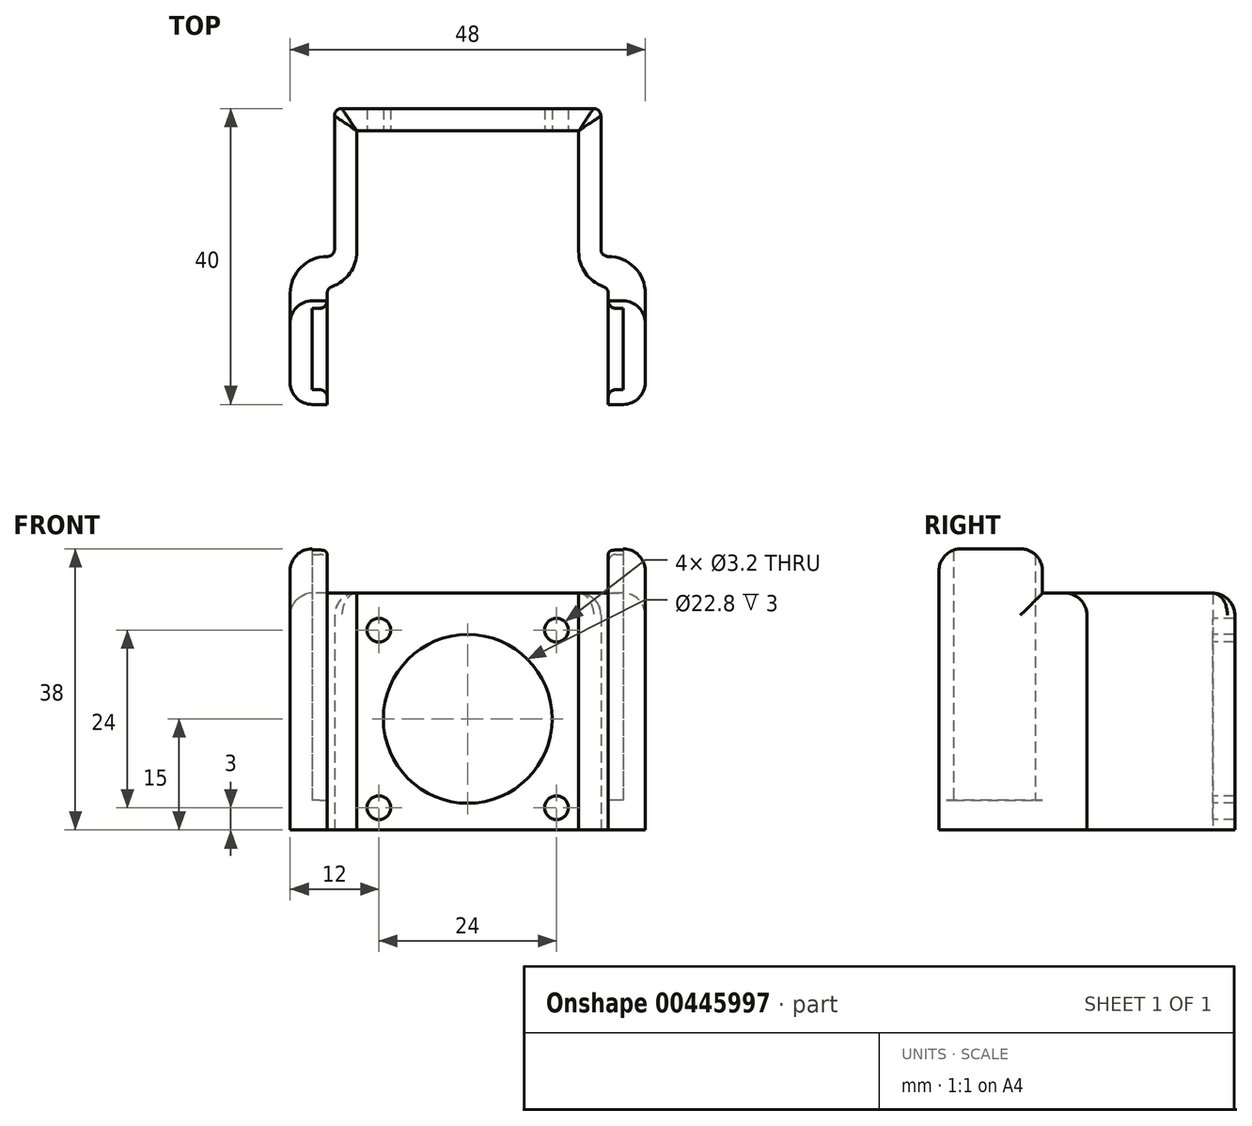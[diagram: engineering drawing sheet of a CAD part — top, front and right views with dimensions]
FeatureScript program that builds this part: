
annotation { "Feature Type Name" : "Feature", "Feature Type Description" : "" }
export const myFeature = defineFeature(function(context is Context, id is Id, definition is map)
    precondition{}
    {
        {
            var Q0;
            Q0=qCreatedBy(makeId("Top.planeOp"),FACE);
            var sketch = newSketch(context, id + "F0", { "sketchPlane" : qUnion([Q0])});
            skLineSegment(sketch, "E0", {"start": v(-29.4, 0) * mm, "end": v(-18, 0) * mm, "construction": true});
            skLineSegment(sketch, "E1.0", {"start": v(-29.4, -20) * mm, "end": v(-19, -20) * mm, "construction": true});
            skLineSegment(sketch, "E2.0", {"start": v(-18, 20) * mm, "end": v(0, 20) * mm, "construction": true});
            skLineSegment(sketch, "E3", {"start": v(0, 32.75) * mm, "end": v(0, -30.7) * mm, "construction": true});
            skLineSegment(sketch, "E4.0", {"start": v(-18, 32.75) * mm, "end": v(-18, 0) * mm, "construction": true});
            skLineSegment(sketch, "E5.trimOffspring", {"start": v(-24, 0) * mm, "end": v(-24, -30.7) * mm, "construction": true});
            skLineSegment(sketch, "E6.0", {"start": v(-15, 17) * mm, "end": v(0, 17) * mm});
            skLineSegment(sketch, "E7.0", {"start": v(-15, 32.75) * mm, "end": v(-15, 20) * mm});
            skLineSegment(sketch, "E8.trimOffspring", {"start": v(-15, 17) * mm, "end": v(-15, 0) * mm});
            skLineSegment(sketch, "E9.0", {"start": v(-29.4, -4) * mm, "end": v(-24, -4) * mm, "construction": true});
            skLineSegment(sketch, "E10", {"start": v(-15, 0) * mm, "end": v(-15, -8.6) * mm, "construction": true});
            skLineSegment(sketch, "E11.0", {"start": v(-21, -4) * mm, "end": v(-21, -30.7) * mm, "construction": true});
            skLineSegment(sketch, "E12.trimOffspring", {"start": v(-21, -4) * mm, "end": v(-15, -4) * mm, "construction": true});
            skLineSegment(sketch, "E13.trimOffspring", {"start": v(-15, 0) * mm, "end": v(35.32, 0) * mm, "construction": true});
            skLineSegment(sketch, "E14.0", {"start": v(-19, -5) * mm, "end": v(-19, -30.7) * mm, "construction": true});
            skLineSegment(sketch, "E15", {"start": v(-24, -20) * mm, "end": v(-19, -20) * mm, "construction": true});
            skLineSegment(sketch, "E16.trimOffspring", {"start": v(0, -20) * mm, "end": v(35.32, -20) * mm, "construction": true});
            skLineSegment(sketch, "E17.0", {"start": v(-24, -18) * mm, "end": v(-19, -18) * mm, "construction": true});
            skLineSegment(sketch, "E18.0", {"start": v(-24, -7) * mm, "end": v(-19, -7) * mm, "construction": true});
            skLineSegment(sketch, "E19", {"start": v(0, 20) * mm, "end": v(-18, 20) * mm});
            skLineSegment(sketch, "E20", {"start": v(-18, 20) * mm, "end": v(-18, 0) * mm});
            skLineSegment(sketch, "E21", {"start": v(-18, 0) * mm, "end": v(-24, 0) * mm});
            skLineSegment(sketch, "E22", {"start": v(-24, 0) * mm, "end": v(-24, -20) * mm});
            skLineSegment(sketch, "E23", {"start": v(-24, -20) * mm, "end": v(-19, -20) * mm});
            skLineSegment(sketch, "E24", {"start": v(-19, -18) * mm, "end": v(-19, -20) * mm});
            skLineSegment(sketch, "E25", {"start": v(-19, -18) * mm, "end": v(-21, -18) * mm});
            skLineSegment(sketch, "E26", {"start": v(-21, -7) * mm, "end": v(-19, -7) * mm});
            skLineSegment(sketch, "E27", {"start": v(-21, -18) * mm, "end": v(-21, -7) * mm});
            skLineSegment(sketch, "E28", {"start": v(-19, -7) * mm, "end": v(-19, -4) * mm});
            skLineSegment(sketch, "E29", {"start": v(-19, -4) * mm, "end": v(-15, -4) * mm});
            skLineSegment(sketch, "E30", {"start": v(-15, 17) * mm, "end": v(-15, -4) * mm});
            skLineSegment(sketch, "E31", {"start": v(-15, -4) * mm, "end": v(-19, -4) * mm});
            skLineSegment(sketch, "E32", {"start": v(0, 20) * mm, "end": v(0, 17) * mm});
            skLineSegment(sketch, "E33.MirrorCS", {"start": v(0, 20) * mm, "end": v(18, 20) * mm});
            skLineSegment(sketch, "E34.MirrorCS", {"start": v(15, 17) * mm, "end": v(0, 17) * mm});
            skLineSegment(sketch, "E35.MirrorCS", {"start": v(15, 17) * mm, "end": v(15, 0) * mm});
            skLineSegment(sketch, "E36.MirrorCS", {"start": v(18, 20) * mm, "end": v(18, 0) * mm});
            skLineSegment(sketch, "E37.MirrorCS", {"start": v(15, 17) * mm, "end": v(15, -4) * mm});
            skLineSegment(sketch, "E38.MirrorCS", {"start": v(18, 0) * mm, "end": v(24, 0) * mm});
            skLineSegment(sketch, "E39.MirrorCS", {"start": v(19, -4) * mm, "end": v(15, -4) * mm});
            skLineSegment(sketch, "E40.MirrorCS", {"start": v(24, 0) * mm, "end": v(24, -20) * mm});
            skLineSegment(sketch, "E41.MirrorCS", {"start": v(24, -20) * mm, "end": v(19, -20) * mm});
            skLineSegment(sketch, "E42.MirrorCS", {"start": v(19, -18) * mm, "end": v(19, -20) * mm});
            skLineSegment(sketch, "E43.MirrorCS", {"start": v(19, -18) * mm, "end": v(21, -18) * mm});
            skLineSegment(sketch, "E44.MirrorCS", {"start": v(21, -18) * mm, "end": v(21, -7) * mm});
            skLineSegment(sketch, "E45.MirrorCS", {"start": v(19, -7) * mm, "end": v(19, -4) * mm});
            skLineSegment(sketch, "E46.MirrorCS", {"start": v(21, -7) * mm, "end": v(19, -7) * mm});
            skLineSegment(sketch, "E47", {"start": v(-19, -7) * mm, "end": v(-19, -18) * mm});
            skLineSegment(sketch, "E48", {"start": v(19, -7) * mm, "end": v(19, -18) * mm});
            skSolve(sketch);
        }
        {
            var Q0;
            Q0=makeQuery(id+"F0.imprint","IMPRINT",FACE,{"disambiguationData":[TD([[makeQuery(id+"F0.imprint","IMPRINT",EDGE,{"derivedFrom":sQuery(id+"F0.wireOp",EDGE,"E32")}),1.0]])]});
            var Q1;
            {var subQ0=sQuery(id+"F0.wireOp",EDGE,"E6.0");Q1=makeQuery(id+"F0.imprint","IMPRINT",FACE,{"disambiguationData":[TD([[makeQuery(id+"F0.imprint","IMPRINT",EDGE,{"derivedFrom":subQ0}),1.0]])]});}
            extrude(context, id + "F1", {"entities" : qUnion([Q0, Q1]), "depth" : 32 * mm});
        }
        {
            var Q0;
            Q0=makeQuery(id+"F0.imprint","IMPRINT",FACE,{"disambiguationData":[TD([[makeQuery(id+"F0.imprint","IMPRINT",EDGE,{"derivedFrom":sQuery(id+"F0.wireOp",EDGE,"E25")}),-1.0]])]});
            var Q1;
            Q1=makeQuery(id+"F0.imprint","IMPRINT",FACE,{"disambiguationData":[TD([[makeQuery(id+"F0.imprint","IMPRINT",EDGE,{"derivedFrom":sQuery(id+"F0.wireOp",EDGE,"E43.MirrorCS")}),1.0]])]});
            extrude(context, id + "F2", {"entities" : qUnion([Q0, Q1]), "operationType" : NewBodyOperationType.ADD, "depth" : 4 * mm});
        }
        {
            var Q0;
            Q0=makeQuery(id+"F1.opExtrude","SWEPT_EDGE",EDGE,{"disambiguationData":[OSD([sQuery(id+"F0.wireOp",EDGE,"E45.MirrorCS"),sQuery(id+"F0.wireOp",EDGE,"E46.MirrorCS"),sQuery(id+"F0.wireOp",EDGE,"E48")])]});
            var Q1;
            Q1=makeQuery(id+"F1.opExtrude","SWEPT_EDGE",EDGE,{"disambiguationData":[OSD([sQuery(id+"F0.wireOp",EDGE,"E42.MirrorCS"),sQuery(id+"F0.wireOp",EDGE,"E43.MirrorCS"),sQuery(id+"F0.wireOp",EDGE,"E48")])]});
            var Q2;
            Q2=makeQuery(id+"F1.opExtrude","SWEPT_EDGE",EDGE,{"disambiguationData":[OSD([sQuery(id+"F0.wireOp",EDGE,"E26"),sQuery(id+"F0.wireOp",EDGE,"E28"),sQuery(id+"F0.wireOp",EDGE,"E47")])]});
            var Q3;
            Q3=makeQuery(id+"F1.opExtrude","SWEPT_EDGE",EDGE,{"disambiguationData":[OSD([sQuery(id+"F0.wireOp",EDGE,"E24"),sQuery(id+"F0.wireOp",EDGE,"E25"),sQuery(id+"F0.wireOp",EDGE,"E47")])]});
            var Q4;
            Q4=makeQuery(id+"F1.opExtrude","SWEPT_EDGE",EDGE,{"disambiguationData":[OSD([sQuery(id+"F0.wireOp",EDGE,"E33.MirrorCS"),sQuery(id+"F0.wireOp",EDGE,"E36.MirrorCS")])]});
            var Q5;
            Q5=makeQuery(id+"F1.opExtrude","SWEPT_EDGE",EDGE,{"disambiguationData":[OSD([sQuery(id+"F0.wireOp",EDGE,"E19"),sQuery(id+"F0.wireOp",EDGE,"E20")])]});
            var Q6;
            Q6=makeQuery(id+"F1.opExtrude","SWEPT_EDGE",EDGE,{"disambiguationData":[OSD([sQuery(id+"F0.wireOp",EDGE,"E20"),sQuery(id+"F0.wireOp",EDGE,"E21")])]});
            var Q7;
            Q7=makeQuery(id+"F1.opExtrude","SWEPT_EDGE",EDGE,{"disambiguationData":[OSD([sQuery(id+"F0.wireOp",EDGE,"E36.MirrorCS"),sQuery(id+"F0.wireOp",EDGE,"E38.MirrorCS")])]});
            var Q8;
            Q8=makeQuery(id+"F1.opExtrude","SWEPT_EDGE",EDGE,{"disambiguationData":[OSD([sQuery(id+"F0.wireOp",EDGE,"E39.MirrorCS"),sQuery(id+"F0.wireOp",EDGE,"E45.MirrorCS")])]});
            var Q9;
            Q9=makeQuery(id+"F1.opExtrude","SWEPT_EDGE",EDGE,{"disambiguationData":[OSD([sQuery(id+"F0.wireOp",EDGE,"E28"),sQuery(id+"F0.wireOp",EDGE,"E31")])]});
            fillet(context, id + "F3", {"entities" : qUnion([Q0, Q1, Q2, Q3, Q4, Q5, Q6, Q7, Q8, Q9]), "radius" : 1 * mm, "tangentPropagation" : true, "allowEdgeOverflow" : false});
        }
        {
            var Q0;
            Q0=makeQuery(id+"F1.opExtrude","SWEPT_EDGE",EDGE,{"disambiguationData":[OSD([sQuery(id+"F0.wireOp",EDGE,"E30"),sQuery(id+"F0.wireOp",EDGE,"E31")])]});
            var Q1;
            Q1=makeQuery(id+"F1.opExtrude","SWEPT_EDGE",EDGE,{"disambiguationData":[OSD([sQuery(id+"F0.wireOp",EDGE,"E38.MirrorCS"),sQuery(id+"F0.wireOp",EDGE,"E40.MirrorCS")])]});
            var Q2;
            Q2=makeQuery(id+"F1.opExtrude","SWEPT_EDGE",EDGE,{"disambiguationData":[OSD([sQuery(id+"F0.wireOp",EDGE,"E21"),sQuery(id+"F0.wireOp",EDGE,"E22")])]});
            var Q3;
            Q3=makeQuery(id+"F1.opExtrude","SWEPT_EDGE",EDGE,{"disambiguationData":[OSD([sQuery(id+"F0.wireOp",EDGE,"E37.MirrorCS"),sQuery(id+"F0.wireOp",EDGE,"E39.MirrorCS")])]});
            fillet(context, id + "F4", {"entities" : qUnion([Q0, Q1, Q2, Q3]), "radius" : 5 * mm, "tangentPropagation" : true, "allowEdgeOverflow" : false});
        }
        {
            var Q0;
            Q0=makeQuery(id+"F1.opExtrude","SWEPT_EDGE",EDGE,{"disambiguationData":[OSD([sQuery(id+"F0.wireOp",EDGE,"E40.MirrorCS"),sQuery(id+"F0.wireOp",EDGE,"E41.MirrorCS")])]});
            var Q1;
            Q1=makeQuery(id+"F1.opExtrude","SWEPT_EDGE",EDGE,{"disambiguationData":[OSD([sQuery(id+"F0.wireOp",EDGE,"E22"),sQuery(id+"F0.wireOp",EDGE,"E23")])]});
            fillet(context, id + "F5", {"entities" : qUnion([Q0, Q1]), "radius" : 3 * mm, "tangentPropagation" : true, "allowEdgeOverflow" : false});
        }
        {
            var Q0;
            Q0=makeQuery(id+"F1.opExtrude","CAP_FACE",FACE,{"disambiguationData":[OSD([sQuery(id+"F0.wireOp",EDGE,"E6.0"),sQuery(id+"F0.wireOp",EDGE,"E19"),sQuery(id+"F0.wireOp",EDGE,"E20"),sQuery(id+"F0.wireOp",EDGE,"E21"),sQuery(id+"F0.wireOp",EDGE,"E22"),sQuery(id+"F0.wireOp",EDGE,"E23"),sQuery(id+"F0.wireOp",EDGE,"E24"),sQuery(id+"F0.wireOp",EDGE,"E25"),sQuery(id+"F0.wireOp",EDGE,"E26"),sQuery(id+"F0.wireOp",EDGE,"E27"),sQuery(id+"F0.wireOp",EDGE,"E28"),sQuery(id+"F0.wireOp",EDGE,"E30"),sQuery(id+"F0.wireOp",EDGE,"E31"),sQuery(id+"F0.wireOp",EDGE,"E33.MirrorCS"),sQuery(id+"F0.wireOp",EDGE,"E34.MirrorCS"),sQuery(id+"F0.wireOp",EDGE,"E36.MirrorCS"),sQuery(id+"F0.wireOp",EDGE,"E37.MirrorCS"),sQuery(id+"F0.wireOp",EDGE,"E38.MirrorCS"),sQuery(id+"F0.wireOp",EDGE,"E39.MirrorCS"),sQuery(id+"F0.wireOp",EDGE,"E40.MirrorCS"),sQuery(id+"F0.wireOp",EDGE,"E41.MirrorCS"),sQuery(id+"F0.wireOp",EDGE,"E42.MirrorCS"),sQuery(id+"F0.wireOp",EDGE,"E43.MirrorCS"),sQuery(id+"F0.wireOp",EDGE,"E44.MirrorCS"),sQuery(id+"F0.wireOp",EDGE,"E45.MirrorCS"),sQuery(id+"F0.wireOp",EDGE,"E46.MirrorCS")])],"isStart":false});
            var sketch = newSketch(context, id + "F6", { "sketchPlane" : qUnion([Q0])});
            skLineSegment(sketch, "E49.0.0", {"start": v(19, -5) * mm, "end": v(19, -6) * mm});
            skArc(sketch, "E49.0.1", {"start": v(19, -6) * mm, "mid": v(19.3, -6.7) * mm, "end": v(20, -7) * mm});
            skLineSegment(sketch, "E49.0.2", {"start": v(20, -7) * mm, "end": v(21, -7) * mm});
            skLineSegment(sketch, "E49.0.3", {"start": v(21, -7) * mm, "end": v(21, -18) * mm});
            skLineSegment(sketch, "E49.0.4", {"start": v(21, -18) * mm, "end": v(20, -18) * mm});
            skArc(sketch, "E49.0.5", {"start": v(20, -18) * mm, "mid": v(19.3, -18.3) * mm, "end": v(19, -19) * mm});
            skLineSegment(sketch, "E49.0.6", {"start": v(19, -19) * mm, "end": v(19, -20) * mm});
            skLineSegment(sketch, "E49.0.7", {"start": v(19, -20) * mm, "end": v(23, -20) * mm});
            skArc(sketch, "E49.0.8", {"start": v(23, -20) * mm, "mid": v(23.7, -19.7) * mm, "end": v(24, -19) * mm});
            skLineSegment(sketch, "E49.0.9", {"start": v(24, -19) * mm, "end": v(24, -1) * mm});
            skArc(sketch, "E49.0.10", {"start": v(24, -1) * mm, "mid": v(23.7, -0.3) * mm, "end": v(23, 0) * mm});
            skLineSegment(sketch, "E49.0.11", {"start": v(23, 0) * mm, "end": v(19, 0) * mm});
            skArc(sketch, "E49.0.12", {"start": v(19, 0) * mm, "mid": v(18.3, 0.3) * mm, "end": v(18, 1) * mm});
            skLineSegment(sketch, "E49.0.13", {"start": v(18, 1) * mm, "end": v(18, 19) * mm});
            skArc(sketch, "E49.0.14", {"start": v(18, 19) * mm, "mid": v(17.7, 19.7) * mm, "end": v(17, 20) * mm});
            skLineSegment(sketch, "E49.0.15", {"start": v(17, 20) * mm, "end": v(-17, 20) * mm});
            skArc(sketch, "E49.0.16", {"start": v(-17, 20) * mm, "mid": v(-17.7, 19.7) * mm, "end": v(-18, 19) * mm});
            skLineSegment(sketch, "E49.0.17", {"start": v(-18, 19) * mm, "end": v(-18, 1) * mm});
            skArc(sketch, "E49.0.18", {"start": v(-18, 1) * mm, "mid": v(-18.3, 0.3) * mm, "end": v(-19, 0) * mm});
            skLineSegment(sketch, "E49.0.19", {"start": v(-19, 0) * mm, "end": v(-23, 0) * mm});
            skArc(sketch, "E49.0.20", {"start": v(-23, 0) * mm, "mid": v(-23.7, -0.3) * mm, "end": v(-24, -1) * mm});
            skLineSegment(sketch, "E49.0.21", {"start": v(-24, -1) * mm, "end": v(-24, -19) * mm});
            skArc(sketch, "E49.0.22", {"start": v(-24, -19) * mm, "mid": v(-23.7, -19.7) * mm, "end": v(-23, -20) * mm});
            skLineSegment(sketch, "E49.0.23", {"start": v(-23, -20) * mm, "end": v(-19, -20) * mm});
            skLineSegment(sketch, "E49.0.24", {"start": v(-19, -20) * mm, "end": v(-19, -19) * mm});
            skArc(sketch, "E49.0.25", {"start": v(-19, -19) * mm, "mid": v(-19.3, -18.3) * mm, "end": v(-20, -18) * mm});
            skLineSegment(sketch, "E49.0.26", {"start": v(-20, -18) * mm, "end": v(-21, -18) * mm});
            skLineSegment(sketch, "E49.0.27", {"start": v(-21, -18) * mm, "end": v(-21, -7) * mm});
            skLineSegment(sketch, "E49.0.28", {"start": v(-21, -7) * mm, "end": v(-20, -7) * mm});
            skArc(sketch, "E49.0.29", {"start": v(-20, -7) * mm, "mid": v(-19.3, -6.7) * mm, "end": v(-19, -6) * mm});
            skLineSegment(sketch, "E49.0.30", {"start": v(-19, -6) * mm, "end": v(-19, -5) * mm});
            skArc(sketch, "E49.0.31", {"start": v(-19, -5) * mm, "mid": v(-18.7, -4.3) * mm, "end": v(-18, -4) * mm});
            skLineSegment(sketch, "E49.0.32", {"start": v(-18, -4) * mm, "end": v(-16, -4) * mm});
            skArc(sketch, "E49.0.33", {"start": v(-16, -4) * mm, "mid": v(-15.3, -3.7) * mm, "end": v(-15, -3) * mm});
            skLineSegment(sketch, "E49.0.34", {"start": v(-15, -3) * mm, "end": v(-15, 17) * mm});
            skLineSegment(sketch, "E49.0.35", {"start": v(-15, 17) * mm, "end": v(15, 17) * mm});
            skLineSegment(sketch, "E49.0.36", {"start": v(15, 17) * mm, "end": v(15, -3) * mm});
            skArc(sketch, "E49.0.37", {"start": v(15, -3) * mm, "mid": v(15.3, -3.7) * mm, "end": v(16, -4) * mm});
            skLineSegment(sketch, "E49.0.38", {"start": v(16, -4) * mm, "end": v(18, -4) * mm});
            skArc(sketch, "E49.0.39", {"start": v(18, -4) * mm, "mid": v(18.7, -4.3) * mm, "end": v(19, -5) * mm});
            skLineSegment(sketch, "E50.0", {"start": v(17, -6) * mm, "end": v(-17, -6) * mm, "construction": true});
            skLineSegment(sketch, "E51", {"start": v(-17, -6) * mm, "end": v(-29.99, -6) * mm});
            skLineSegment(sketch, "E52", {"start": v(-29.99, -6) * mm, "end": v(26.5, -6) * mm});
            skSolve(sketch);
        }
        {
            var Q0;
            {var subQ0=sQuery(id+"F6.wireOp",EDGE,"E49.0.1");Q0=makeQuery(id+"F6.imprint","IMPRINT",FACE,{"disambiguationData":[TD([[makeQuery(id+"F6.imprint","IMPRINT",EDGE,{"derivedFrom":subQ0}),1.0]])]});}
            var Q1;
            {var subQ0=sQuery(id+"F6.wireOp",EDGE,"E49.0.24");Q1=makeQuery(id+"F6.imprint","IMPRINT",FACE,{"disambiguationData":[TD([[makeQuery(id+"F6.imprint","IMPRINT",EDGE,{"derivedFrom":subQ0}),-1.0]])]});}
            extrude(context, id + "F7", {"entities" : qUnion([Q0, Q1]), "operationType" : NewBodyOperationType.ADD, "depth" : 6 * mm});
        }
        {
            var Q0;
            Q0=makeQuery(id+"F1.opExtrude","SWEPT_FACE",FACE,{"disambiguationData":[OSD([sQuery(id+"F0.wireOp",EDGE,"E6.0"),sQuery(id+"F0.wireOp",EDGE,"E34.MirrorCS")])]});
            var sketch = newSketch(context, id + "F8", { "sketchPlane" : qUnion([Q0])});
            skLineSegment(sketch, "E53.0.0", {"start": v(-15, 0) * mm, "end": v(15, 0) * mm});
            skLineSegment(sketch, "E53.0.1", {"start": v(15, 0) * mm, "end": v(15, 32) * mm});
            skLineSegment(sketch, "E53.0.2", {"start": v(15, 32) * mm, "end": v(-15, 32) * mm});
            skLineSegment(sketch, "E53.0.3", {"start": v(-15, 32) * mm, "end": v(-15, 0) * mm});
            skLineSegment(sketch, "E54", {"start": v(0, 0) * mm, "end": v(0, 32) * mm, "construction": true});
            skLineSegment(sketch, "E55.0", {"start": v(12, 0) * mm, "end": v(12, 32) * mm, "construction": true});
            skLineSegment(sketch, "E56.0", {"start": v(-15, 15) * mm, "end": v(15, 15) * mm, "construction": true});
            skLineSegment(sketch, "E57.0", {"start": v(-15, 3) * mm, "end": v(15, 3) * mm, "construction": true});
            skCircle(sketch, "E58", {"center": v(12, 3) * mm, "radius": 1.6 * mm});
            skCircle(sketch, "E59.1.0", {"center": v(12, 27) * mm, "radius": 1.6 * mm});
            skCircle(sketch, "E59.2.0", {"center": v(-12, 27) * mm, "radius": 1.6 * mm});
            skCircle(sketch, "E59.3.0", {"center": v(-12, 3) * mm, "radius": 1.6 * mm});
            skPoint(sketch, "E59.center", {"position": v(0, 15) * mm});
            skCircle(sketch, "E60", {"center": v(0, 15) * mm, "radius": 11.4 * mm});
            skSolve(sketch);
        }
        {
            var Q0;
            Q0=makeQuery(id+"F8.imprint","IMPRINT",FACE,{"disambiguationData":[TD([[makeQuery(id+"F8.imprint","IMPRINT",EDGE,{"derivedFrom":sQuery(id+"F8.wireOp",EDGE,"E58")}),1.0]])]});
            var Q1;
            Q1=makeQuery(id+"F8.imprint","IMPRINT",FACE,{"disambiguationData":[TD([[makeQuery(id+"F8.imprint","IMPRINT",EDGE,{"derivedFrom":sQuery(id+"F8.wireOp",EDGE,"E59.3.0")}),1.0]])]});
            var Q2;
            Q2=makeQuery(id+"F8.imprint","IMPRINT",FACE,{"disambiguationData":[TD([[makeQuery(id+"F8.imprint","IMPRINT",EDGE,{"derivedFrom":sQuery(id+"F8.wireOp",EDGE,"E59.1.0")}),1.0]])]});
            var Q3;
            Q3=makeQuery(id+"F8.imprint","IMPRINT",FACE,{"disambiguationData":[TD([[makeQuery(id+"F8.imprint","IMPRINT",EDGE,{"derivedFrom":sQuery(id+"F8.wireOp",EDGE,"E59.2.0")}),1.0]])]});
            var Q4;
            Q4=makeQuery(id+"F8.imprint","IMPRINT",FACE,{"disambiguationData":[TD([[makeQuery(id+"F8.imprint","IMPRINT",EDGE,{"derivedFrom":sQuery(id+"F8.wireOp",EDGE,"E60")}),1.0]])]});
            extrude(context, id + "F9", {"entities" : qUnion([Q0, Q1, Q2, Q3, Q4]), "operationType" : NewBodyOperationType.REMOVE, "oppositeDirection" : true, "depth" : 25 * mm});
        }
        {
            var Q0;
            Q0=makeQuery(id+"F7.opExtrude","SWEPT_EDGE",EDGE,{"disambiguationData":[OSD([sQuery(id+"F6.wireOp",EDGE,"E49.0.21"),sQuery(id+"F6.wireOp",EDGE,"E52")])]});
            var Q1;
            Q1=makeQuery(id+"F7.opExtrude","SWEPT_EDGE",EDGE,{"disambiguationData":[OSD([sQuery(id+"F6.wireOp",EDGE,"E49.0.9"),sQuery(id+"F6.wireOp",EDGE,"E52")])]});
            fillet(context, id + "F10", {"entities" : qUnion([Q0, Q1]), "radius" : 3 * mm, "tangentPropagation" : true, "allowEdgeOverflow" : false});
        }
        {
            var Q0;
            Q0=makeQuery(id+"F1.opExtrude","CAP_EDGE",EDGE,{"disambiguationData":[OSD([sQuery(id+"F0.wireOp",EDGE,"E20")])],"isStart":false});
            var Q1;
            Q1=makeQuery(id+"F1.opExtrude","CAP_EDGE",EDGE,{"disambiguationData":[OSD([sQuery(id+"F0.wireOp",EDGE,"E36.MirrorCS")])],"isStart":false});
            var Q2;
            {var subQ0=sQuery(id+"F0.wireOp",EDGE,"E40.MirrorCS");var subQ1=sQuery(id+"F0.wireOp",EDGE,"E38.MirrorCS");Q2=makeQuery(id+"F4.opFillet","BLEND_EDGE",EDGE,{"blendedFrom":[makeQuery(id+"F1.opExtrude","SWEPT_EDGE",EDGE,{"disambiguationData":[OSD([subQ1,subQ0])]}),makeQuery(id+"F1.opExtrude","CAP_FACE",FACE,{"disambiguationData":[OSD([sQuery(id+"F0.wireOp",EDGE,"E6.0"),sQuery(id+"F0.wireOp",EDGE,"E19"),sQuery(id+"F0.wireOp",EDGE,"E20"),sQuery(id+"F0.wireOp",EDGE,"E21"),sQuery(id+"F0.wireOp",EDGE,"E22"),sQuery(id+"F0.wireOp",EDGE,"E23"),sQuery(id+"F0.wireOp",EDGE,"E24"),sQuery(id+"F0.wireOp",EDGE,"E25"),sQuery(id+"F0.wireOp",EDGE,"E26"),sQuery(id+"F0.wireOp",EDGE,"E27"),sQuery(id+"F0.wireOp",EDGE,"E28"),sQuery(id+"F0.wireOp",EDGE,"E30"),sQuery(id+"F0.wireOp",EDGE,"E31"),sQuery(id+"F0.wireOp",EDGE,"E33.MirrorCS"),sQuery(id+"F0.wireOp",EDGE,"E34.MirrorCS"),sQuery(id+"F0.wireOp",EDGE,"E36.MirrorCS"),sQuery(id+"F0.wireOp",EDGE,"E37.MirrorCS"),subQ1,sQuery(id+"F0.wireOp",EDGE,"E39.MirrorCS"),subQ0,sQuery(id+"F0.wireOp",EDGE,"E41.MirrorCS"),sQuery(id+"F0.wireOp",EDGE,"E42.MirrorCS"),sQuery(id+"F0.wireOp",EDGE,"E43.MirrorCS"),sQuery(id+"F0.wireOp",EDGE,"E44.MirrorCS"),sQuery(id+"F0.wireOp",EDGE,"E45.MirrorCS"),sQuery(id+"F0.wireOp",EDGE,"E46.MirrorCS")])],"isStart":false})],"blendedInto":[makeQuery(id+"F1.opExtrude","CAP_FACE",FACE,{"disambiguationData":[OSD([sQuery(id+"F0.wireOp",EDGE,"E6.0"),sQuery(id+"F0.wireOp",EDGE,"E19"),sQuery(id+"F0.wireOp",EDGE,"E20"),sQuery(id+"F0.wireOp",EDGE,"E21"),sQuery(id+"F0.wireOp",EDGE,"E22"),sQuery(id+"F0.wireOp",EDGE,"E23"),sQuery(id+"F0.wireOp",EDGE,"E24"),sQuery(id+"F0.wireOp",EDGE,"E25"),sQuery(id+"F0.wireOp",EDGE,"E26"),sQuery(id+"F0.wireOp",EDGE,"E27"),sQuery(id+"F0.wireOp",EDGE,"E28"),sQuery(id+"F0.wireOp",EDGE,"E30"),sQuery(id+"F0.wireOp",EDGE,"E31"),sQuery(id+"F0.wireOp",EDGE,"E33.MirrorCS"),sQuery(id+"F0.wireOp",EDGE,"E34.MirrorCS"),sQuery(id+"F0.wireOp",EDGE,"E36.MirrorCS"),sQuery(id+"F0.wireOp",EDGE,"E37.MirrorCS"),subQ1,sQuery(id+"F0.wireOp",EDGE,"E39.MirrorCS"),subQ0,sQuery(id+"F0.wireOp",EDGE,"E41.MirrorCS"),sQuery(id+"F0.wireOp",EDGE,"E42.MirrorCS"),sQuery(id+"F0.wireOp",EDGE,"E43.MirrorCS"),sQuery(id+"F0.wireOp",EDGE,"E44.MirrorCS"),sQuery(id+"F0.wireOp",EDGE,"E45.MirrorCS"),sQuery(id+"F0.wireOp",EDGE,"E46.MirrorCS")])],"isStart":false})]});}
            var Q3;
            {var subQ0=sQuery(id+"F0.wireOp",EDGE,"E22");var subQ1=sQuery(id+"F0.wireOp",EDGE,"E21");Q3=makeQuery(id+"F4.opFillet","BLEND_EDGE",EDGE,{"blendedFrom":[makeQuery(id+"F1.opExtrude","SWEPT_EDGE",EDGE,{"disambiguationData":[OSD([subQ1,subQ0])]}),makeQuery(id+"F1.opExtrude","CAP_FACE",FACE,{"disambiguationData":[OSD([sQuery(id+"F0.wireOp",EDGE,"E6.0"),sQuery(id+"F0.wireOp",EDGE,"E19"),sQuery(id+"F0.wireOp",EDGE,"E20"),subQ1,subQ0,sQuery(id+"F0.wireOp",EDGE,"E23"),sQuery(id+"F0.wireOp",EDGE,"E24"),sQuery(id+"F0.wireOp",EDGE,"E25"),sQuery(id+"F0.wireOp",EDGE,"E26"),sQuery(id+"F0.wireOp",EDGE,"E27"),sQuery(id+"F0.wireOp",EDGE,"E28"),sQuery(id+"F0.wireOp",EDGE,"E30"),sQuery(id+"F0.wireOp",EDGE,"E31"),sQuery(id+"F0.wireOp",EDGE,"E33.MirrorCS"),sQuery(id+"F0.wireOp",EDGE,"E34.MirrorCS"),sQuery(id+"F0.wireOp",EDGE,"E36.MirrorCS"),sQuery(id+"F0.wireOp",EDGE,"E37.MirrorCS"),sQuery(id+"F0.wireOp",EDGE,"E38.MirrorCS"),sQuery(id+"F0.wireOp",EDGE,"E39.MirrorCS"),sQuery(id+"F0.wireOp",EDGE,"E40.MirrorCS"),sQuery(id+"F0.wireOp",EDGE,"E41.MirrorCS"),sQuery(id+"F0.wireOp",EDGE,"E42.MirrorCS"),sQuery(id+"F0.wireOp",EDGE,"E43.MirrorCS"),sQuery(id+"F0.wireOp",EDGE,"E44.MirrorCS"),sQuery(id+"F0.wireOp",EDGE,"E45.MirrorCS"),sQuery(id+"F0.wireOp",EDGE,"E46.MirrorCS")])],"isStart":false})],"blendedInto":[makeQuery(id+"F1.opExtrude","CAP_FACE",FACE,{"disambiguationData":[OSD([sQuery(id+"F0.wireOp",EDGE,"E6.0"),sQuery(id+"F0.wireOp",EDGE,"E19"),sQuery(id+"F0.wireOp",EDGE,"E20"),subQ1,subQ0,sQuery(id+"F0.wireOp",EDGE,"E23"),sQuery(id+"F0.wireOp",EDGE,"E24"),sQuery(id+"F0.wireOp",EDGE,"E25"),sQuery(id+"F0.wireOp",EDGE,"E26"),sQuery(id+"F0.wireOp",EDGE,"E27"),sQuery(id+"F0.wireOp",EDGE,"E28"),sQuery(id+"F0.wireOp",EDGE,"E30"),sQuery(id+"F0.wireOp",EDGE,"E31"),sQuery(id+"F0.wireOp",EDGE,"E33.MirrorCS"),sQuery(id+"F0.wireOp",EDGE,"E34.MirrorCS"),sQuery(id+"F0.wireOp",EDGE,"E36.MirrorCS"),sQuery(id+"F0.wireOp",EDGE,"E37.MirrorCS"),sQuery(id+"F0.wireOp",EDGE,"E38.MirrorCS"),sQuery(id+"F0.wireOp",EDGE,"E39.MirrorCS"),sQuery(id+"F0.wireOp",EDGE,"E40.MirrorCS"),sQuery(id+"F0.wireOp",EDGE,"E41.MirrorCS"),sQuery(id+"F0.wireOp",EDGE,"E42.MirrorCS"),sQuery(id+"F0.wireOp",EDGE,"E43.MirrorCS"),sQuery(id+"F0.wireOp",EDGE,"E44.MirrorCS"),sQuery(id+"F0.wireOp",EDGE,"E45.MirrorCS"),sQuery(id+"F0.wireOp",EDGE,"E46.MirrorCS")])],"isStart":false})]});}
            var Q4;
            Q4=makeQuery(id+"F7.opExtrude","CAP_EDGE",EDGE,{"disambiguationData":[OSD([sQuery(id+"F6.wireOp",EDGE,"E49.0.21")])],"isStart":false});
            var Q5;
            Q5=makeQuery(id+"F7.opExtrude","CAP_EDGE",EDGE,{"disambiguationData":[OSD([sQuery(id+"F6.wireOp",EDGE,"E49.0.9")])],"isStart":false});
            fillet(context, id + "F11", {"entities" : qUnion([Q0, Q1, Q2, Q3, Q4, Q5]), "radius" : 3 * mm, "tangentPropagation" : true, "allowEdgeOverflow" : false});
        }
    });
